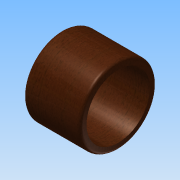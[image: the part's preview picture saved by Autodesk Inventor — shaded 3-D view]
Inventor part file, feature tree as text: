
AUTODESK INVENTOR PART (.ipt)
format: ipt  version: 2015 (Build 190159000, 159)  size: 142,848 bytes
history: native  units: in
note: dims shown in document units (in); Inventor stores cm internally (conversion verified against a paired STEP export)
features: revolve x1, fillet x1, sketch x1
ambient origin geometry x8: Origin, YZ Plane, XZ Plane, XY Plane, X Axis, Y Axis, Z Axis, Center Point
bodies: Solid1 (feature_tree)
feature tree (3):
  revolve  "Revolution1"  [1 undecoded]
  fillet  "Fillet1"  Radius=0.5392in
  sketch  "Sketch1"  dims[d0=4.469in d1=0.156in d2=0.5392in d3=1.8229in d5=90.0deg d6=0.25in]
note: 1 required parameter value undecoded (feature->parameter linkage not recoverable at this tier; creation-order binding heuristic only, values carry confidence <= 0.55)
